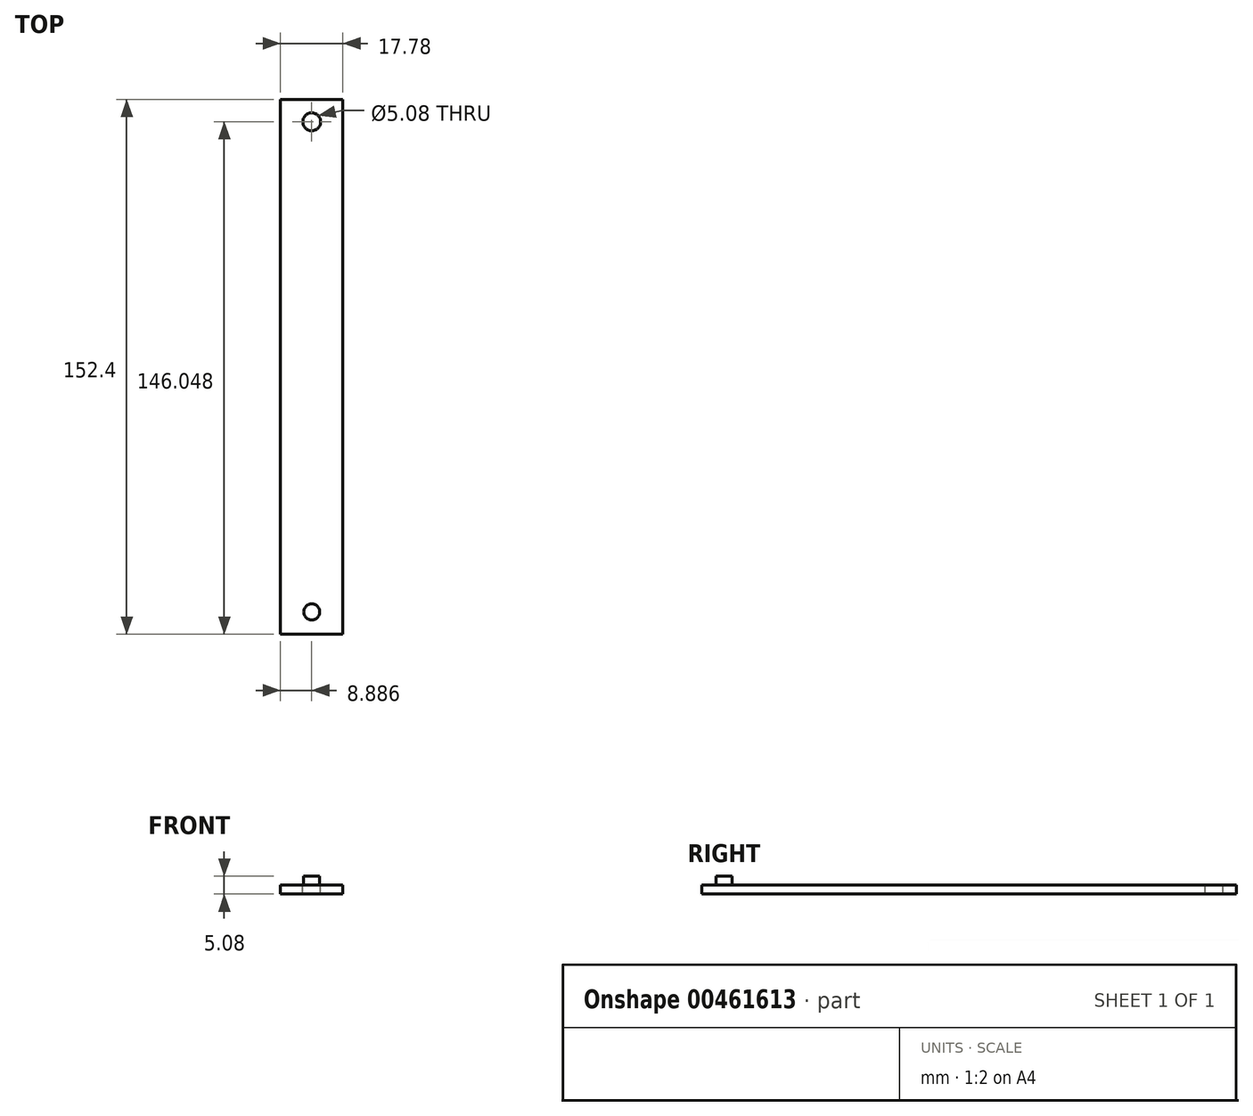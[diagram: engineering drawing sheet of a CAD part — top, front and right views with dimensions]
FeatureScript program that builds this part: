
annotation { "Feature Type Name" : "Feature", "Feature Type Description" : "" }
export const myFeature = defineFeature(function(context is Context, id is Id, definition is map)
    precondition{}
    {
        {
            var Q0;
            Q0=qCreatedBy(makeId("Top.planeOp"),FACE);
            var sketch = newSketch(context, id + "F0", { "sketchPlane" : qUnion([Q0])});
            skLineSegment(sketch, "E0.bottom", {"start": v(-16.93, -8.82) * mm, "end": v(0.85, -8.82) * mm});
            skLineSegment(sketch, "E0.top", {"start": v(-16.93, 143.58) * mm, "end": v(0.85, 143.58) * mm});
            skLineSegment(sketch, "E0.left", {"start": v(-16.93, -8.82) * mm, "end": v(-16.93, 143.58) * mm});
            skLineSegment(sketch, "E0.right", {"start": v(0.85, -8.82) * mm, "end": v(0.85, 143.58) * mm});
            skSolve(sketch);
        }
        {
            var Q0;
            Q0=qSketchRegion(id+"F0",true);
            extrude(context, id + "F1", {"entities" : qUnion([Q0]), "depth" : 2.54 * mm});
        }
        {
            var Q0;
            Q0=makeQuery(id+"F1.opExtrude","CAP_FACE",FACE,{"disambiguationData":[OSD([sQuery(id+"F0.wireOp",EDGE,"E0.bottom"),sQuery(id+"F0.wireOp",EDGE,"E0.top"),sQuery(id+"F0.wireOp",EDGE,"E0.left"),sQuery(id+"F0.wireOp",EDGE,"E0.right")])],"isStart":false});
            var sketch = newSketch(context, id + "F2", { "sketchPlane" : qUnion([Q0])});
            skLineSegment(sketch, "E1", {"start": v(-8.04, 143.58) * mm, "end": v(-8.04, 137.23) * mm});
            skCircle(sketch, "E2", {"center": v(-8.04, 137.23) * mm, "radius": 2.54 * mm});
            skSolve(sketch);
        }
        {
            var Q0;
            Q0=qSketchRegion(id+"F2",true);
            extrude(context, id + "F3", {"entities" : qUnion([Q0]), "operationType" : NewBodyOperationType.REMOVE, "endBound" : BoundingType.THROUGH_ALL, "oppositeDirection" : true, "depth" : 25.4 * mm});
        }
        {
            var Q0;
            Q0=makeQuery(id+"F1.opExtrude","CAP_FACE",FACE,{"disambiguationData":[OSD([sQuery(id+"F0.wireOp",EDGE,"E0.bottom"),sQuery(id+"F0.wireOp",EDGE,"E0.top"),sQuery(id+"F0.wireOp",EDGE,"E0.left"),sQuery(id+"F0.wireOp",EDGE,"E0.right")])],"isStart":false});
            var sketch = newSketch(context, id + "F4", { "sketchPlane" : qUnion([Q0])});
            skLineSegment(sketch, "E3", {"start": v(-8.04, -8.82) * mm, "end": v(-8.04, -2.47) * mm});
            skCircle(sketch, "E4", {"center": v(-8.04, -2.47) * mm, "radius": 2.29 * mm});
            skSolve(sketch);
        }
        {
            var Q0;
            Q0=qSketchRegion(id+"F4",true);
            extrude(context, id + "F5", {"entities" : qUnion([Q0]), "operationType" : NewBodyOperationType.ADD, "depth" : 2.54 * mm});
        }
    });
